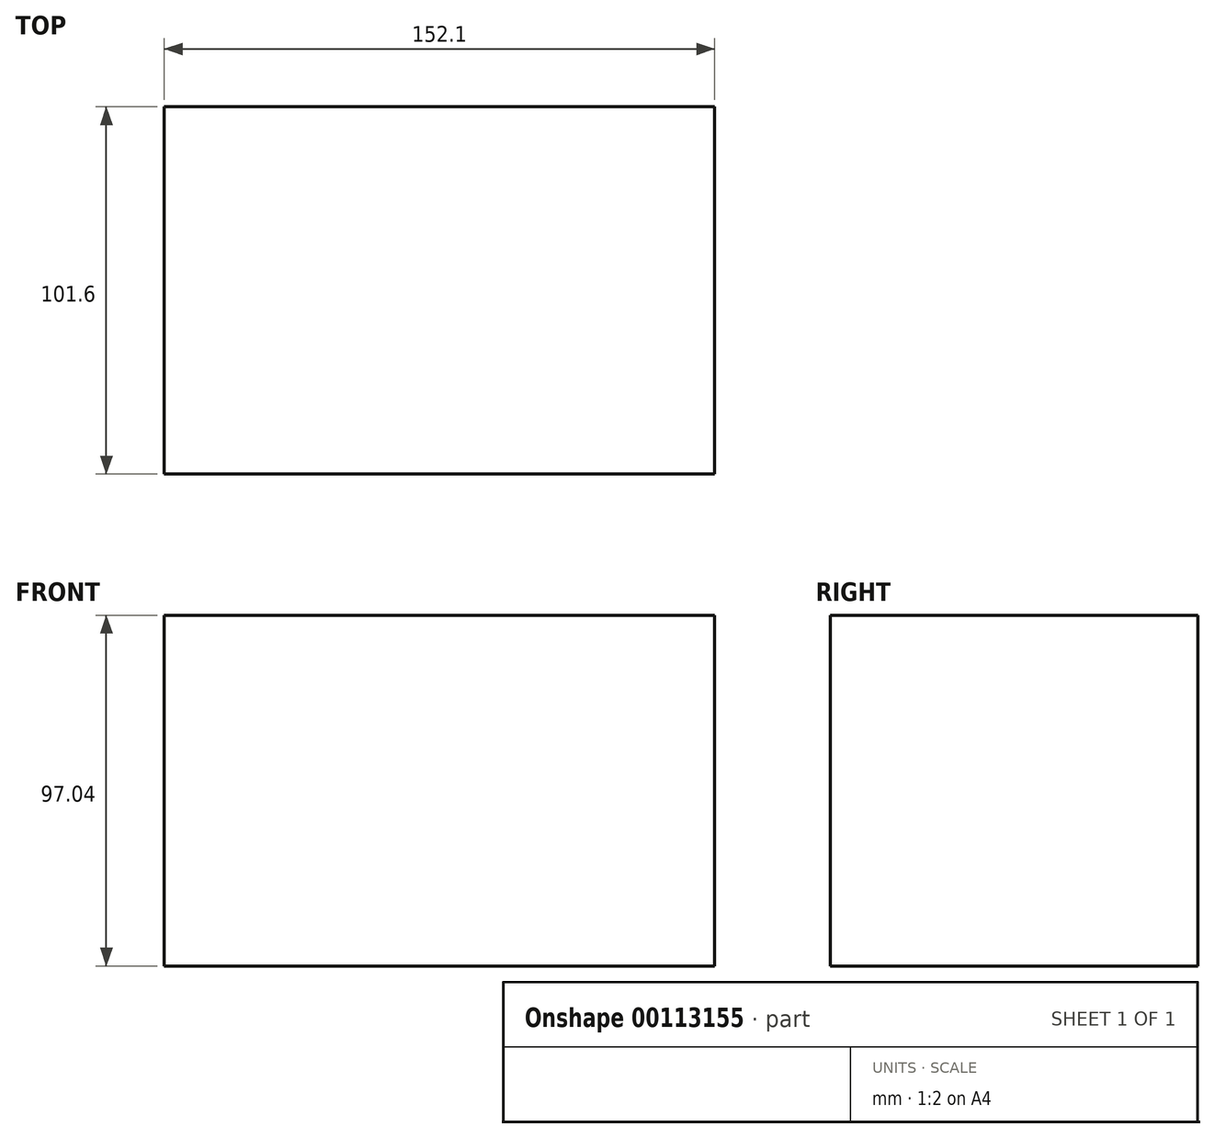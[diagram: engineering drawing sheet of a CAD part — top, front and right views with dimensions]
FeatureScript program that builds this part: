
annotation { "Feature Type Name" : "Feature", "Feature Type Description" : "" }
export const myFeature = defineFeature(function(context is Context, id is Id, definition is map)
    precondition{}
    {
        {
            var Q0;
            Q0=qCreatedBy(makeId("Front.planeOp"),FACE);
            var sketch = newSketch(context, id + "F0", { "sketchPlane" : qUnion([Q0])});
            skLineSegment(sketch, "E0.bottom", {"start": v(-71.74, 0) * mm, "end": v(80.36, 0) * mm});
            skLineSegment(sketch, "E0.top", {"start": v(-71.74, -97.04) * mm, "end": v(80.36, -97.04) * mm});
            skLineSegment(sketch, "E0.left", {"start": v(-71.74, 0) * mm, "end": v(-71.74, -97.04) * mm});
            skLineSegment(sketch, "E0.right", {"start": v(80.36, 0) * mm, "end": v(80.36, -97.04) * mm});
            skSolve(sketch);
        }
        {
            var Q0;
            Q0=makeQuery(id+"F0.imprint","IMPRINT",FACE,{"disambiguationData":[TD([[makeQuery(id+"F0.imprint","IMPRINT",EDGE,{"derivedFrom":sQuery(id+"F0.wireOp",EDGE,"E0.bottom")}),-1.0]])]});
            extrude(context, id + "F1", {"entities" : qUnion([Q0]), "depth" : 101.6 * mm});
        }
    });
